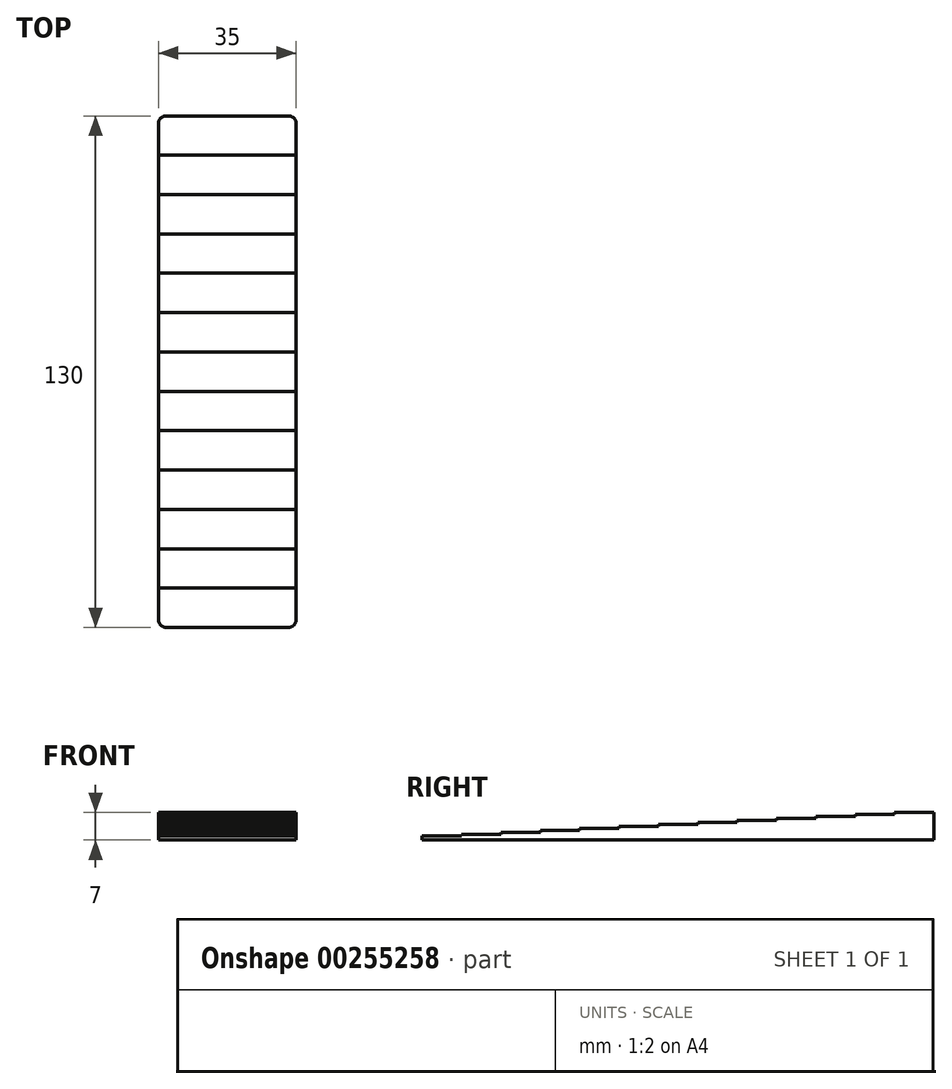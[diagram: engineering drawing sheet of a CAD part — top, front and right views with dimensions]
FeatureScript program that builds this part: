
annotation { "Feature Type Name" : "Feature", "Feature Type Description" : "" }
export const myFeature = defineFeature(function(context is Context, id is Id, definition is map)
    precondition{}
    {
        {
            var Q0;
            Q0=qCreatedBy(makeId("Right.planeOp"),FACE);
            var sketch = newSketch(context, id + "F0", { "sketchPlane" : qUnion([Q0])});
            skLineSegment(sketch, "E0", {"start": v(-60, 4) * mm, "end": v(-70, 4) * mm});
            skLineSegment(sketch, "E1", {"start": v(-70, 4) * mm, "end": v(-70, 3.5) * mm});
            skLineSegment(sketch, "E2", {"start": v(-70, 3.5) * mm, "end": v(-80, 3.5) * mm});
            skLineSegment(sketch, "E3", {"start": v(-80, 3.5) * mm, "end": v(-80, 3) * mm});
            skLineSegment(sketch, "E4", {"start": v(-80, 3) * mm, "end": v(-90, 3) * mm});
            skLineSegment(sketch, "E5", {"start": v(-90, 3) * mm, "end": v(-90, 2.5) * mm});
            skLineSegment(sketch, "E6", {"start": v(-90, 2.5) * mm, "end": v(-100, 2.5) * mm});
            skLineSegment(sketch, "E7", {"start": v(-100, 2.5) * mm, "end": v(-100, 2) * mm});
            skLineSegment(sketch, "E8", {"start": v(-100, 2) * mm, "end": v(-110, 2) * mm});
            skLineSegment(sketch, "E9", {"start": v(-110, 2) * mm, "end": v(-110, 1.5) * mm});
            skLineSegment(sketch, "E10", {"start": v(-110, 1.5) * mm, "end": v(-120, 1.5) * mm});
            skLineSegment(sketch, "E11", {"start": v(-120, 1.5) * mm, "end": v(-120, 1) * mm});
            skLineSegment(sketch, "E12", {"start": v(-120, 1) * mm, "end": v(-130, 1) * mm});
            skLineSegment(sketch, "E13", {"start": v(-130, 1) * mm, "end": v(-130, 0) * mm});
            skLineSegment(sketch, "E14", {"start": v(-60, 4) * mm, "end": v(-60, 4.5) * mm});
            skLineSegment(sketch, "E15", {"start": v(-60, 4.5) * mm, "end": v(-50, 4.5) * mm});
            skLineSegment(sketch, "E16", {"start": v(-50, 4.5) * mm, "end": v(-50, 5) * mm});
            skLineSegment(sketch, "E17", {"start": v(-50, 5) * mm, "end": v(-40, 5) * mm});
            skLineSegment(sketch, "E18", {"start": v(-40, 5) * mm, "end": v(-40, 5.5) * mm});
            skLineSegment(sketch, "E19", {"start": v(-40, 5.5) * mm, "end": v(-30, 5.5) * mm});
            skLineSegment(sketch, "E20", {"start": v(-30, 5.5) * mm, "end": v(-30, 6) * mm});
            skLineSegment(sketch, "E21", {"start": v(-30, 6) * mm, "end": v(-20, 6) * mm});
            skLineSegment(sketch, "E22", {"start": v(-20, 6) * mm, "end": v(-20, 6.5) * mm});
            skLineSegment(sketch, "E23", {"start": v(-20, 6.5) * mm, "end": v(-10, 6.5) * mm});
            skLineSegment(sketch, "E24", {"start": v(-10, 6.5) * mm, "end": v(-10, 7) * mm});
            skLineSegment(sketch, "E25", {"start": v(-10, 7) * mm, "end": v(0, 7) * mm});
            skLineSegment(sketch, "E26", {"start": v(-130, 0) * mm, "end": v(0, 0) * mm});
            skLineSegment(sketch, "E27", {"start": v(0, 0) * mm, "end": v(0, 7) * mm});
            skSolve(sketch);
        }
        {
            var Q0;
            Q0 = qSketchRegion(id + "F0", true);
            extrude(context, id + "F1", {"entities" : qUnion([Q0]), "depth" : 35 * mm});
        }
        {
            var Q0;
            Q0=makeQuery(id+"F1.opExtrude","CAP_EDGE",EDGE,{"disambiguationData":[OSD([sQuery(id+"F0.wireOp",EDGE,"E27")])],"isStart":false});
            var Q1;
            Q1=makeQuery(id+"F1.opExtrude","CAP_EDGE",EDGE,{"disambiguationData":[OSD([sQuery(id+"F0.wireOp",EDGE,"E13")])],"isStart":false});
            var Q2;
            Q2=makeQuery(id+"F1.opExtrude","CAP_EDGE",EDGE,{"disambiguationData":[OSD([sQuery(id+"F0.wireOp",EDGE,"E13")])],"isStart":true});
            var Q3;
            Q3=makeQuery(id+"F1.opExtrude","CAP_EDGE",EDGE,{"disambiguationData":[OSD([sQuery(id+"F0.wireOp",EDGE,"E27")])],"isStart":true});
            fillet(context, id + "F2", {"entities" : qUnion([Q0, Q1, Q2, Q3]), "radius" : 2 * mm, "tangentPropagation" : true, "allowEdgeOverflow" : false});
        }
    });
